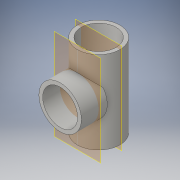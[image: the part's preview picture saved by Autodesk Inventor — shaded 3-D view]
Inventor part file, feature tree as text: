
AUTODESK INVENTOR PART (.ipt)
format: ipt  version: 2016 (Build 200138000, 138)  size: 141,312 bytes
history: native  units: in
note: dims shown in document units (in); Inventor stores cm internally (conversion verified against a paired STEP export)
features: extrude x3, sketch x3, plane x1
ambient origin geometry x8: Origin, YZ Plane, XZ Plane, XY Plane, X Axis, Y Axis, Z Axis, Center Point
bodies: Solid1 (feature_tree)
feature tree (7):
  extrude  "Extrusion1"  Depth=1.315in
  plane  "Work Plane1"
  extrude  "Extrusion2"  Depth=1.315in
  extrude  "Extrusion3"  Depth=0.65in TaperAngle=0.0deg
  sketch  "Sketch1"  dims[d0=1.6in d1=1.315in]
  sketch  "Sketch2"  dims[d2=3.112in d3=0.0in d4=1.315in]
  sketch  "Sketch3"  dims[d5=1.6in d6=0.65in d7=0.325in d8=0.0in d9=0.0in d10=1.315in d11=1.0in d12=0.0in]
